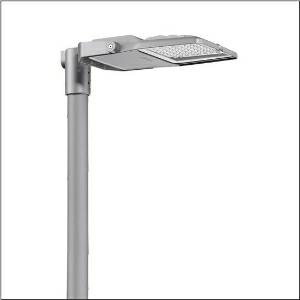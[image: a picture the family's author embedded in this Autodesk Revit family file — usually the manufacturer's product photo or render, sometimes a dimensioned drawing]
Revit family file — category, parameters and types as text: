
# Revit family: floodlight_fl_21_iq_mini___pl43_5xa7771d4a3a_2bc1
name_source: partatom
category: Lighting Fixtures
units: mm (PartAtom-declared; Revit-internal decimal feet)

## family parameters
Cut with Voids When Loaded = No
Host = Face
Light Source = No
Part Type = Normal
Room Calculation Point = No
Round Connector Dimension = Use Diameter
Shared = No

## types (1)
- --- (1 x LED, 19090 lm, 143 W, 4000K)
    Apparent Load = 143 VA
    CIE Flux Codes = 27 78 99 100 100
    Color Rendering = 70
    Color Temperature = 4000K
    Default Elevation = 1800 mm
    Description = Floodlight FL 21 iQ mini, floodlight, primary light control with lens, of PMMA, primary optical cover: protective disc, of toughened safety glass, transparent, light distribution: PL43, light emission: direct distribution, installation type: surface-mounted, LED, High Power LED, rated luminous flux: 19.090lm, luminous efficacy: 134lm/W, light colour: 740, colour temperature: 4000K, control gear: iQ Comfort/DALI, control: Auto-Match, Temp-Guard, Lumen-Switch, Night-Set, Smart-Wire, Light-Fading, Desk-Remote (wireless, voltage-free reading and setting of iQ features in the workshop via application-optimized NFC function/RFID function), optimised constant luminous flux control (CLO 2.0), with terminal, 6-pole, mains connection: 220..240V, AC, 50/60Hz, start of lifetime: 143W, end of service life: 152W, reduction: 61W, luminaire housing, of diecast aluminium, powder-coated, Siteco® metallic grey (DB 702S), corrosivity category C5 mid according to DIN EN ISO 12944, suitable for swimming pools, chlorine-resistant, sealing non-destructively replaceable, please order mast flange separately, mast bracket, of steel, galvanised, powder-coated, Siteco® metallic grey (DB 702S), protection rating (complete): IP66, insulation class (complete): insulation class II (safety insulation), certification: CE, ENEC, VDE, protection symbol: D, impact resistance: IK08, permissible operating ambient temperature: -40..+40°C, permissible operating ambient temperature for outdoor applications: -40..+50°C, standard: DIN EN 12944, LABS conformity tested according to VDMA 24364:2018-05, packaging unit: 1 piece

Light Distribution: PL43
    Height = 70 mm
    Lamp = 1 x LED
    Lamp Light Flux = 19090 lm
    Lamp Power = 143 W
    Lamp count = 1
    Length = 485 mm
    Luminous efficacy = 133 lm/W
    Manufacturer = Siteco
    ModVariant = No
    Model = 5XA7771D4A3A
    Number of Poles = 1
    OnlyDefault = Yes
    Power Factor = 1
    Product Name = Floodlight FL 21 iQ mini | PL43
    Product group = floodlight | pylon annexe
    ProductGroupID = 6200
    Protection Class = Protection class II
    Protection Degree = IP 66
    RLX_Detail_Level = 1
    RLX_Emergency_Light_Flux = 0 lm
    RLX_Emergency_Type = 0
    RLX_Emergency_Type_DB = No
    RlxData = <blob elided: 101637 chars, md5=f3241083>
    Socket = socket
    Standby Power = 0 W
    System Light Flux = 19090 lm
    System Power = 143 W
    Type Comments = factory setting: luminous flux: 100 % | dim-lin: 254 | 730 mA
    Type Image = l_1007125.jpg
    URL = http://relux.com
    VarID = @adj_161754
    Voltage = 0 V
    Weight = 0.00 kg
    Width = 337 mm

## geometry (parser evidence)
native form markers: Blend x4, Sweep x12
no freeform markers — native parametric forms only
